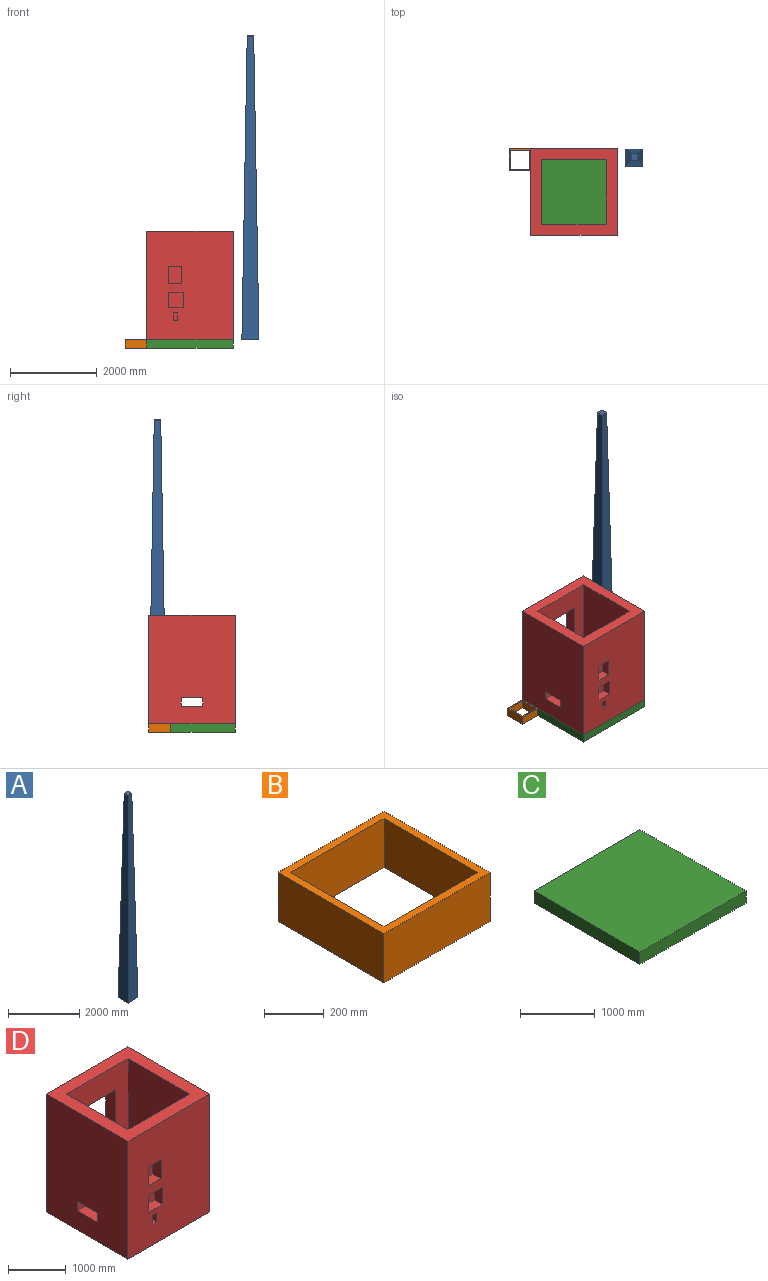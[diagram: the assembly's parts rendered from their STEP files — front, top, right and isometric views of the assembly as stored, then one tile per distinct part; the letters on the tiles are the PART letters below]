
ASSEMBLY  parts=4 mates=3
PART A: 10 faces, bbox 394.4x394.4x7020 mm
  f0: plane 150x20mm, normal (0,-1,0), area 3000mm2, adj f1,f3,f4,f9
  f1: plane 150x20mm, normal (1,0,0), area 3000mm2, adj f0,f2,f4,f8
  f2: plane 150x20mm, normal (0,1,0), area 3000mm2, adj f1,f3,f4,f7
  f3: plane 150x20mm, normal (-1,0,0), area 3000mm2, adj f0,f2,f4,f6
  f4: plane 150x150mm, normal (0,0,1), area 22500mm2, adj f0,f1,f2,f3
  f5: plane 394.37x394.37mm, normal (0,0,-1), area 155528.4mm2, adj f6,f7,f8,f9
  f6: plane 7000x394.37mm, normal (-1,0,0.02), area 1905588.4mm2, adj f3,f5,f7,f9
  f7: plane 7000x394.37mm, normal (0,1,0.02), area 1905588.4mm2, adj f2,f5,f6,f8
  f8: plane 7000x394.37mm, normal (1,0,0.02), area 1905588.4mm2, adj f1,f5,f7,f9
  f9: plane 7000x394.37mm, normal (0,-1,0.02), area 1905588.4mm2, adj f0,f5,f6,f8
PART B: 10 faces, bbox 500x500x200 mm
  f0: plane 440x200mm, normal (0,1,0), area 88000mm2, adj f1,f7,f8,f9
  f1: plane 440x200mm, normal (1,0,0), area 88000mm2, adj f0,f2,f8,f9
  f2: plane 440x200mm, normal (0,-1,0), area 88000mm2, adj f1,f7,f8,f9
  f3: plane 500x200mm, normal (-1,0,0), area 100000mm2, adj f4,f6,f8,f9
  f4: plane 500x200mm, normal (0,-1,0), area 100000mm2, adj f3,f5,f8,f9
  f5: plane 500x200mm, normal (1,0,0), area 100000mm2, adj f4,f6,f8,f9
  f6: plane 500x200mm, normal (0,1,0), area 100000mm2, adj f3,f5,f8,f9
  f7: plane 440x200mm, normal (-1,0,0), area 88000mm2, adj f0,f2,f8,f9
  f8: plane 500x500mm, normal (0,0,1), area 56400mm2, adj f0,f1,f2,f3,f4,f5,f6,f7
  f9: plane 500x500mm, normal (0,0,-1), area 56400mm2, adj f0,f1,f2,f3,f4,f5,f6,f7
PART C: 6 faces, bbox 2000x2000x200 mm
  f0: plane 2000x200mm, normal (0,-1,0), area 400000mm2, adj f1,f3,f4,f5
  f1: plane 2000x200mm, normal (1,0,0), area 400000mm2, adj f0,f2,f4,f5
  f2: plane 2000x200mm, normal (0,1,0), area 400000mm2, adj f1,f3,f4,f5
  f3: plane 2000x200mm, normal (-1,0,0), area 400000mm2, adj f0,f2,f4,f5
  f4: plane 2000x2000mm, normal (0,0,1), area 4000000mm2, adj f0,f1,f2,f3
  f5: plane 2000x2000mm, normal (0,0,-1), area 4000000mm2, adj f0,f1,f2,f3
PART D: 41 faces, bbox 2000x2000x2500 mm
  f0: plane 2500x2000mm, normal (1,0,0), area 4900000mm2, adj f4,f5,f8,f9,f37,f38,f39,f40
  f1: plane 2500x1500mm, normal (-1,0,0), area 3650000mm2, adj f6,f7,f8,f9,f37,f38,f39,f40
  f2: plane 2500x1500mm, normal (1,0,0), area 3237500mm2, adj f6,f7,f8,f9,f23,f24,f25,f26
  f3: plane 2500x2000mm, normal (-1,0,0), area 4900000mm2, adj f4,f5,f8,f9,f33,f34,f35,f36
  f4: plane 2500x2000mm, normal (0,-1,0), area 4732717mm2, adj f0,f3,f8,f9,f13,f14,f15,f16
  f5: plane 2500x2000mm, normal (0,1,0), area 3206256.4mm2, adj f0,f3,f8,f9,f10,f11,f12
  f6: plane 2500x1500mm, normal (0,-1,0), area 1956256.4mm2, adj f1,f2,f8,f9,f10,f11,f12
  f7: plane 2500x1500mm, normal (0,1,0), area 3750000mm2, adj f1,f2,f8,f9
  f8: plane 2000x2000mm, normal (0,0,1), area 1750000mm2, adj f0,f1,f2,f3,f4,f5,f6,f7
  f9: plane 2000x2000mm, normal (0,0,-1), area 1525000mm2, adj f0,f1,f2,f3,f4,f5,f6,f7
  f10: plane 1993.05x250mm, normal (1,0,0), area 498262.1mm2, adj f5,f6,f9,f11
  f11: plane 900x250mm, normal (0,0,-1), area 225000mm2, adj f5,f6,f10,f12
  f12: plane 1993.05x250mm, normal (-1,0,0), area 498262.1mm2, adj f5,f6,f9,f11
  f13: plane 310x200mm, normal (0,0,-1), area 62000mm2, adj f4,f14,f16,f17
  f14: plane 400x200mm, normal (1,0,0), area 80000mm2, adj f4,f13,f15,f17
  f15: plane 310x200mm, normal (0,0,1), area 62000mm2, adj f4,f14,f16,f17
  f16: plane 400x200mm, normal (-1,0,0), area 80000mm2, adj f4,f13,f15,f17
  f17: plane 400x310mm, normal (0,-1,0), area 124000mm2, adj f13,f14,f15,f16
  f18: plane 343x200mm, normal (0,0,-1), area 68600mm2, adj f4,f19,f21,f22
  f19: plane 366x200mm, normal (1,0,0), area 73200mm2, adj f4,f18,f20,f22
  f20: plane 343x200mm, normal (0,0,1), area 68600mm2, adj f4,f19,f21,f22
  f21: plane 366x200mm, normal (-1,0,0), area 73200mm2, adj f4,f18,f20,f22
  f22: plane 366x343mm, normal (0,-1,0), area 125538mm2, adj f18,f19,f20,f21
  f23: plane 550x200mm, normal (0,0,-1), area 110000mm2, adj f2,f24,f26,f27
  f24: plane 750x200mm, normal (0,1,0), area 150000mm2, adj f2,f23,f25,f27
  f25: plane 550x200mm, normal (0,0,1), area 110000mm2, adj f2,f24,f26,f27
  f26: plane 750x200mm, normal (0,-1,0), area 150000mm2, adj f2,f23,f25,f27
  f27: plane 750x550mm, normal (1,0,0), area 412500mm2, adj f23,f24,f25,f26
  f28: plane 100x97.5mm, normal (0,0,-1), area 9750mm2, adj f4,f29,f31,f32
  f29: plane 182x100mm, normal (1,0,0), area 18200mm2, adj f4,f28,f30,f32
  f30: plane 100x97.5mm, normal (0,0,1), area 9750mm2, adj f4,f29,f31,f32
  f31: plane 182x100mm, normal (-1,0,0), area 18200mm2, adj f4,f28,f30,f32
  f32: plane 182x97.5mm, normal (0,-1,0), area 17745mm2, adj f28,f29,f30,f31
  f33: plane 500x250mm, normal (0,0,-1), area 125000mm2, adj f2,f3,f34,f36
  f34: plane 250x200mm, normal (0,-1,0), area 50000mm2, adj f2,f3,f33,f35
  f35: plane 500x250mm, normal (0,0,1), area 125000mm2, adj f2,f3,f34,f36
  f36: plane 250x200mm, normal (0,1,0), area 50000mm2, adj f2,f3,f33,f35
  f37: plane 250x200mm, normal (0,-1,0), area 50000mm2, adj f0,f1,f38,f40
  f38: plane 500x250mm, normal (0,0,-1), area 125000mm2, adj f0,f1,f37,f39
  f39: plane 250x200mm, normal (0,1,0), area 50000mm2, adj f0,f1,f38,f40
  f40: plane 500x250mm, normal (0,0,1), area 125000mm2, adj f0,f1,f37,f39
PLACE A t=(472.19,1722.19,7200)mm
PLACE B t=(-2250,1750,0)mm
PLACE C at identity
PLACE D t=(0,0,200)mm
MATE fastened B.f8 <-> C.f4  axis (0,0,1) through (-2000,2000,200)mm
MATE fastened D.f9 <-> C.f4  axis (0,0,-1) through (0,0,200)mm
MATE fastened A.f5 <-> C.f4  axis (0,0,1) through (200,1600,200)mm
